# Revit family: Bathtub-American_Standard-Studio-2573_Series
name_source: partatom
category: Plumbing Fixtures
revit_build: Autodesk Revit 2014 (Build: 20130308_1515(x64)
units: mm (PartAtom-declared; Revit-internal decimal feet)

## types (4) — shared parameters
Assembly Code = D2010510
CW Connection = Yes
CWFU = 3
Cold Water Connection Diameter = 1/2"
Default Elevation = 0"
Description = Studio Bathing Pool Above Floor Rough with Built-In Apron
Drain Length = 14 5/8"
EverClean Surface = Yes
HW Connection = Yes
HWFU = 3
Height = 18"
Hot Water Connection Diameter = 1/2"
Installation Type = Surface Mounted
Length = 30"
Manufacturer = American Standard
Price = Prices may vary. Please consult Manufacturer Representative for most up-to-date price list.
URL = http://www.americanstandard-us.com
Vent Connection = No
WFU = 4
Warranty Information = Limited Lifetime Warranty
Waste Connection = Yes
Waste Connection Diameter = 1 3/4"
Width = 60"

## per-type parameters (varying)
| type | Drain Offset | Finish | Left Overflow Offset | Material | Right Overflow Offset |
| 2573102.020 | 50 1/4" | High Gloss Acrylic-American Standard-020-White | 1" | High Gloss Acrylic-American Standard-020-White | 5" |
| 2573102.011 | 50 1/4" | High Gloss Acrylic-American Standard-011-Arctic White | 1" | High Gloss Acrylic-American Standard-011-Arctic White | 5" |
| 2573202.020 | 9 3/4" | High Gloss Acrylic-American Standard-020-White | 5" | High Gloss Acrylic-American Standard-020-White | 1" |
| 2573202.011 | 9 3/4" | High Gloss Acrylic-American Standard-011-Arctic White | 5" | High Gloss Acrylic-American Standard-011-Arctic White | 1" |

note: column(s) folded — value = type name in every type: Model

## geometry (parser evidence)
native form markers: Sweep x1
no freeform markers — native parametric forms only
